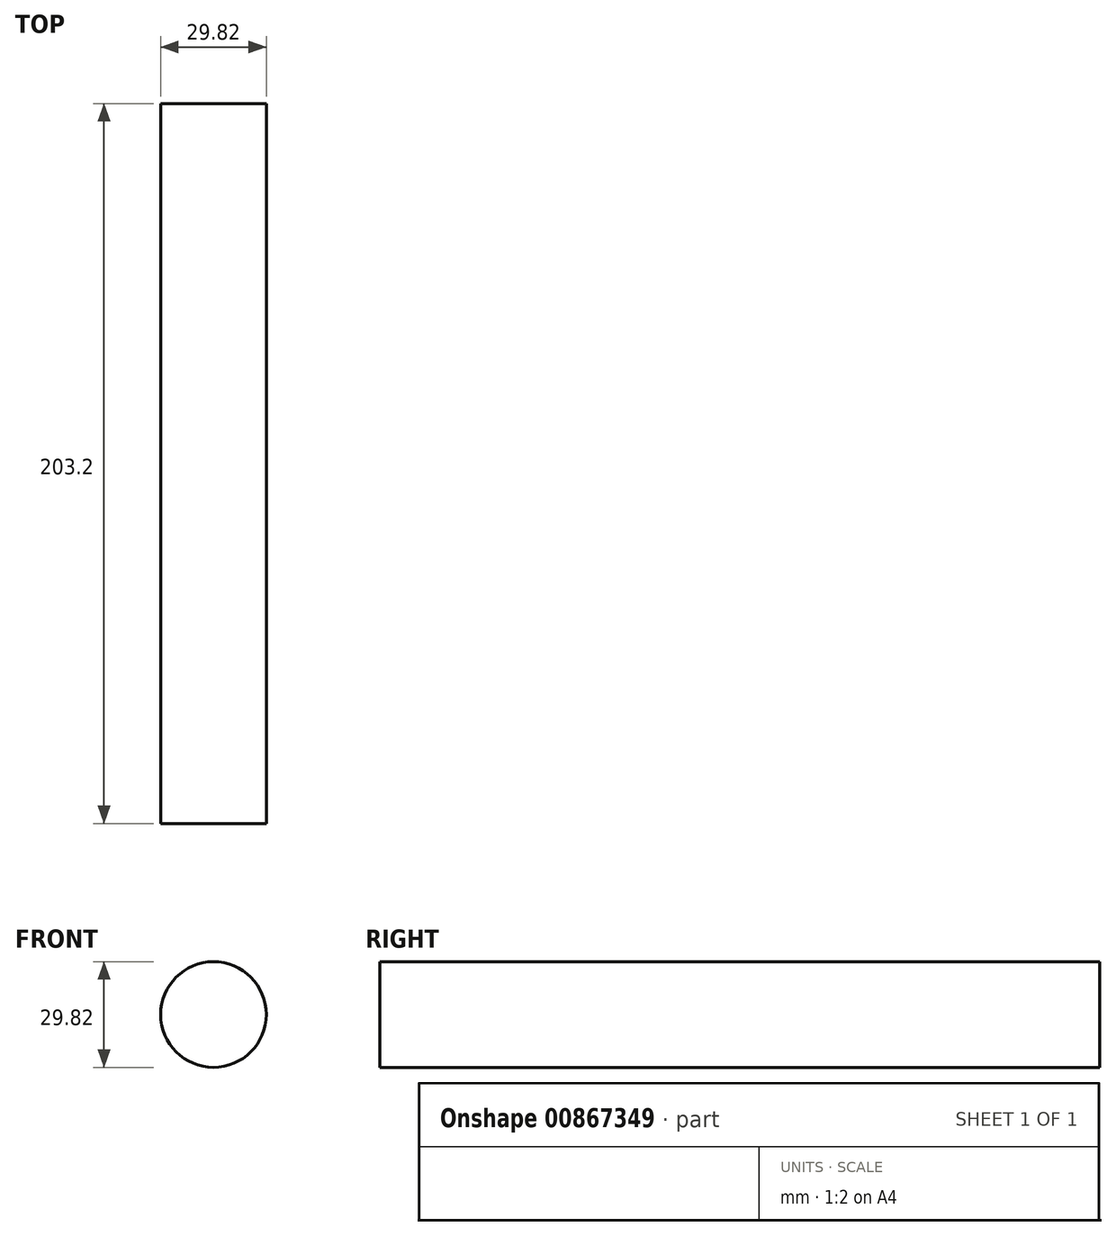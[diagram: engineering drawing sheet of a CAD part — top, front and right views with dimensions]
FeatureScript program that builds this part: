
annotation { "Feature Type Name" : "Feature", "Feature Type Description" : "" }
export const myFeature = defineFeature(function(context is Context, id is Id, definition is map)
    precondition{}
    {
        {
            var Q0;
            Q0=qCreatedBy(makeId("Front.planeOp"),FACE);
            var sketch = newSketch(context, id + "F0", { "sketchPlane" : qUnion([Q0])});
            skCircle(sketch, "E0", {"center": v(0, 0) * mm, "radius": 14.9 * mm});
            skSolve(sketch);
        }
        {
            var Q0;
            Q0 = qSketchRegion(id + "F0", true);
            extrude(context, id + "F1", {"entities" : qUnion([Q0]), "depth" : 203.2 * mm, "offsetDistance" : 25.4 * mm});
        }
    });
